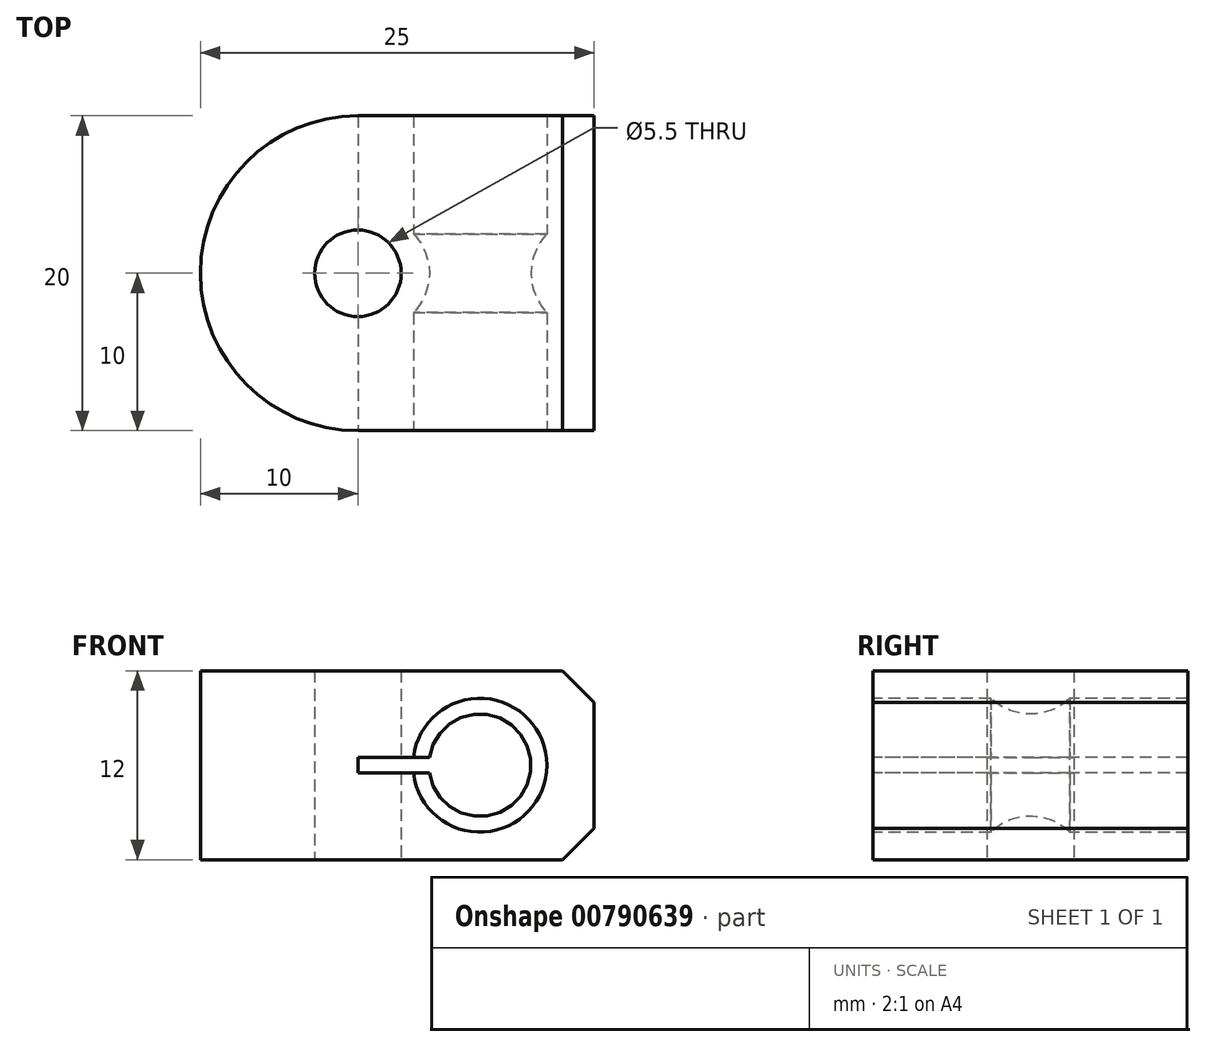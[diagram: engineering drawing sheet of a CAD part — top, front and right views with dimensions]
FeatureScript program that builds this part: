
annotation { "Feature Type Name" : "Feature", "Feature Type Description" : "" }
export const myFeature = defineFeature(function(context is Context, id is Id, definition is map)
    precondition{}
    {
        {
            var Q0;
            Q0=qCreatedBy(makeId("Top.planeOp"),FACE);
            var sketch = newSketch(context, id + "F0", { "sketchPlane" : qUnion([Q0])});
            skArc(sketch, "E0", {"start": v(0, 10) * mm, "mid": v(-10, 0) * mm, "end": v(0, -10) * mm});
            skCircle(sketch, "E1", {"center": v(0, 0) * mm, "radius": 2.75 * mm});
            skLineSegment(sketch, "E2.bottom", {"start": v(0, 10) * mm, "end": v(15, 10) * mm});
            skLineSegment(sketch, "E2.top", {"start": v(0, -10) * mm, "end": v(15, -10) * mm});
            skLineSegment(sketch, "E2.left", {"start": v(0, 10) * mm, "end": v(0, -10) * mm});
            skLineSegment(sketch, "E2.right", {"start": v(15, 10) * mm, "end": v(15, -10) * mm});
            skSolve(sketch);
        }
        {
            var Q0;
            {var subQ1=sQuery(id+"F0.wireOp",EDGE,"E2.bottom");Q0=makeQuery(id+"F0.imprint","IMPRINT",FACE,{"disambiguationData":[TD([[makeQuery(id+"F0.imprint","IMPRINT",EDGE,{"derivedFrom":subQ1}),-1.0]])]});}
            var Q1;
            {var subQ0=sQuery(id+"F0.wireOp",EDGE,"E0");Q1=makeQuery(id+"F0.imprint","IMPRINT",FACE,{"disambiguationData":[TD([[makeQuery(id+"F0.imprint","IMPRINT",EDGE,{"derivedFrom":subQ0}),1.0]])]});}
            extrude(context, id + "F1", {"entities" : qUnion([Q0, Q1]), "depth" : 12 * mm, "offsetDistance" : 25 * mm});
        }
        {
            var Q0;
            Q0=makeQuery(id+"F1.opExtrude","SWEPT_FACE",FACE,{"disambiguationData":[OSD([sQuery(id+"F0.wireOp",EDGE,"E2.top")])]});
            var sketch = newSketch(context, id + "F2", { "sketchPlane" : qUnion([Q0])});
            skLineSegment(sketch, "E3", {"start": v(15, 6) * mm, "end": v(-27.82, 6) * mm, "construction": true});
            skLineSegment(sketch, "E4.bottom", {"start": v(7.75, 5.5) * mm, "end": v(-10, 5.5) * mm});
            skLineSegment(sketch, "E4.top", {"start": v(7.75, 6.5) * mm, "end": v(-10, 6.5) * mm});
            skLineSegment(sketch, "E4.left", {"start": v(7.75, 5.5) * mm, "end": v(7.75, 6.5) * mm});
            skLineSegment(sketch, "E4.right", {"start": v(-10, 5.5) * mm, "end": v(-10, 6.5) * mm});
            skPoint(sketch, "E4.middle", {"position": v(-1.13, 6) * mm});
            skLineSegment(sketch, "E5", {"start": v(-10, 0) * mm, "end": v(-10, 11) * mm});
            skCircle(sketch, "E6", {"center": v(7.75, 6) * mm, "radius": 4.25 * mm});
            skSolve(sketch);
        }
        {
            var Q0;
            {var subQ0=sQuery(id+"F2.wireOp",EDGE,"E4.left");Q0=makeQuery(id+"F2.imprint","IMPRINT",FACE,{"disambiguationData":[TD([[makeQuery(id+"F2.imprint","IMPRINT",EDGE,{"derivedFrom":subQ0}),-1.0]])]});}
            var Q1;
            {var subQ0=sQuery(id+"F2.wireOp",EDGE,"E4.left");Q1=makeQuery(id+"F2.imprint","IMPRINT",FACE,{"disambiguationData":[TD([[makeQuery(id+"F2.imprint","IMPRINT",EDGE,{"derivedFrom":subQ0}),1.0]])]});}
            extrude(context, id + "F3", {"entities" : qUnion([Q0, Q1]), "operationType" : NewBodyOperationType.REMOVE, "endBound" : BoundingType.THROUGH_ALL, "oppositeDirection" : true, "depth" : 25 * mm, "offsetDistance" : 25 * mm});
        }
        {
            var Q0;
            Q0=makeQuery(id+"F1.opExtrude","CAP_EDGE",EDGE,{"disambiguationData":[OSD([sQuery(id+"F0.wireOp",EDGE,"E2.right")])],"isStart":true});
            var Q1;
            Q1=makeQuery(id+"F1.opExtrude","CAP_EDGE",EDGE,{"disambiguationData":[OSD([sQuery(id+"F0.wireOp",EDGE,"E2.right")])],"isStart":false});
            chamfer(context, id + "F4", {"entities" : qUnion([Q0, Q1]), "width" : 2 * mm, "tangentPropagation" : true});
        }
        {
            var Q0;
            Q0=makeQuery(id+"F1.opExtrude","CAP_FACE",FACE,{"disambiguationData":[OSD([sQuery(id+"F0.wireOp",EDGE,"E0"),sQuery(id+"F0.wireOp",EDGE,"E1"),sQuery(id+"F0.wireOp",EDGE,"E2.bottom"),sQuery(id+"F0.wireOp",EDGE,"E2.top"),sQuery(id+"F0.wireOp",EDGE,"E2.right")])],"isStart":false});
            var Q1;
            {var subQ1=sQuery(id+"F0.wireOp",EDGE,"E2.bottom");Q1=makeQuery(id+"F0.imprint","IMPRINT",FACE,{"disambiguationData":[TD([[makeQuery(id+"F0.imprint","IMPRINT",EDGE,{"derivedFrom":subQ1}),-1.0]])]});}
            cPlane(context, id + "F5", {"entities" : qUnion([Q0, Q1]), "cplaneType" : CPlaneType.MID_PLANE, "offset" : 25 * mm, "width" : 150 * mm, "height" : 150 * mm});
        }
        {
            var Q0;
            Q0=qCreatedBy(id+"F5.planeOp",FACE);
            var sketch = newSketch(context, id + "F6", { "sketchPlane" : qUnion([Q0])});
            skArc(sketch, "E7", {"start": v(3.5, -2.5) * mm, "mid": v(4.5, 0) * mm, "end": v(3.5, 2.5) * mm});
            skPoint(sketch, "E8", {"position": v(4.5, 0) * mm});
            skLineSegment(sketch, "E9.0", {"start": v(3.5, -10) * mm, "end": v(3.5, 9.99) * mm});
            skLineSegment(sketch, "E10.0", {"start": v(12, -10) * mm, "end": v(3.5, -10) * mm});
            skSolve(sketch);
        }
        {
            var Q0;
            Q0=qCreatedBy(makeId("Front.planeOp"),FACE);
            var sketch = newSketch(context, id + "F7", { "sketchPlane" : qUnion([Q0])});
            skArc(sketch, "E11.0", {"start": v(3.65, 4.9) * mm, "mid": v(11.96, 6.56) * mm, "end": v(3.5, 6) * mm});
            skArc(sketch, "E12.0.0", {"start": v(3.53, 5.5) * mm, "mid": v(12, 6) * mm, "end": v(3.53, 6.5) * mm});
            skLineSegment(sketch, "E12.0.1", {"start": v(3.53, 6.5) * mm, "end": v(7.75, 6.5) * mm});
            skLineSegment(sketch, "E12.0.2", {"start": v(7.75, 6.5) * mm, "end": v(7.75, 5.5) * mm});
            skLineSegment(sketch, "E12.0.3", {"start": v(7.75, 5.5) * mm, "end": v(3.53, 5.5) * mm});
            skCircle(sketch, "E13", {"center": v(7.75, 6) * mm, "radius": 4.25 * mm});
            skSolve(sketch);
        }
        {
            var Q0;
            {var subQ0=sQuery(id+"F6.wireOp",EDGE,"E7");Q0=makeQuery(id+"F6.imprint","IMPRINT",FACE,{"disambiguationData":[TD([[makeQuery(id+"F6.imprint","IMPRINT",EDGE,{"derivedFrom":subQ0}),1.0]])]});}
            var Q1;
            Q1=sQuery(id+"F7.wireOp",EDGE,"E13");
            sweep(context, id + "F8", {"operationType" : NewBodyOperationType.ADD, "profiles" : qUnion([Q0]), "path" : qUnion([Q1])});
        }
        {
            var Q0;
            {var subQ0=sQuery(id+"F2.wireOp",EDGE,"E4.left");Q0=makeQuery(id+"F2.imprint","IMPRINT",FACE,{"disambiguationData":[TD([[makeQuery(id+"F2.imprint","IMPRINT",EDGE,{"derivedFrom":subQ0}),1.0]])]});}
            var Q1;
            {var subQ0=sQuery(id+"F2.wireOp",EDGE,"E6");var subQ1=sQuery(id+"F2.wireOp",EDGE,"E4.bottom");var subQ2=makeQuery(id+"F2.imprint","INTERSECT",VERTEX,{"derivedFrom":[subQ1,subQ0]});Q1=makeQuery(id+"F2.imprint","IMPRINT",FACE,{"disambiguationData":[TD([[makeQuery(id+"F2.imprint","IMPRINT",EDGE,{"disambiguationData":[TD([[subQ2,1.0]])],"derivedFrom":subQ0}),-1.0]])]});}
            var Q2;
            {var subQ0=sQuery(id+"F2.wireOp",EDGE,"E5");var subQ1=sQuery(id+"F2.wireOp",EDGE,"E4.bottom");var subQ2=makeQuery(id+"F2.imprint","INTERSECT",VERTEX,{"derivedFrom":[subQ1,subQ0]});Q2=makeQuery(id+"F2.imprint","IMPRINT",FACE,{"disambiguationData":[TD([[makeQuery(id+"F2.imprint","IMPRINT",EDGE,{"disambiguationData":[TD([[subQ2,-1.0]])],"derivedFrom":subQ0}),-1.0]])]});}
            extrude(context, id + "F9", {"entities" : qUnion([Q0, Q1, Q2]), "operationType" : NewBodyOperationType.REMOVE, "oppositeDirection" : true, "depth" : 25 * mm, "offsetDistance" : 25 * mm});
        }
    });
